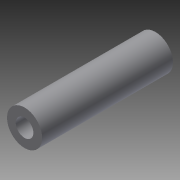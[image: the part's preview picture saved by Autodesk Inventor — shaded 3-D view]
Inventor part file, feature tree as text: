
AUTODESK INVENTOR PART (.ipt)
format: ipt  version: 2014 SP2 (Build 180246200, 246)  size: 95,744 bytes
history: native  units: in
note: dims shown in document units (in); Inventor stores cm internally (conversion verified against a paired STEP export)
features: other x7, sketch x2, revolve x1, hole x1
ambient origin geometry x8: Origin, YZ Plane, XZ Plane, XY Plane, X Axis, Y Axis, Z Axis, Center Point
bodies: Solid1 (feature_tree)
feature tree (11):
  revolve  "Revolution1"  [1 undecoded]
  hole  "Hole1"  [1 undecoded]
  other  "screw_XY"
  other  "screw_YZ"
  other  "screw_ZX"
  other  "screw_X"
  other  "screw_Y"
  other  "screw_Z"
  other  "screw_Center"
  sketch  "Sketch_1"  dims[d0=360.0deg]
  sketch  "Sketch2"  dims[d1=0.118in d2=0.75in d3=0.375in d4=0.25in d5=0.5635in d6=0.875in d7=0.0in d8=0.0in]
note: 2 required parameter values undecoded (feature->parameter linkage not recoverable at this tier; creation-order binding heuristic only, values carry confidence <= 0.55)